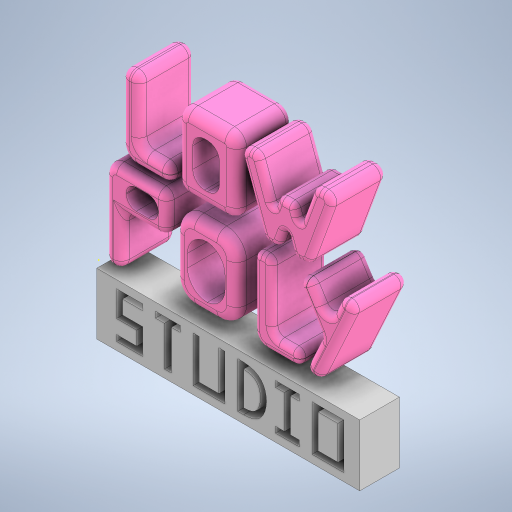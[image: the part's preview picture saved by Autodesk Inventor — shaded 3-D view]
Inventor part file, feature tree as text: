
AUTODESK INVENTOR PART (.ipt)
format: ipt  version: 2024.1 (Build 281209000, 209)  size: 1,081,856 bytes
history: native  units: mm
features: fillet x23, sketch x5, extrude x4, projected_geometry x1
ambient origin geometry x8: Origin, YZ Plane, XZ Plane, XY Plane, X Axis, Y Axis, Z Axis, Center Point
bodies: Solid2 (feature_tree)
feature tree (33):
  extrude  "Extrusion6"  Depth=10.0mm TaperAngle=0.0deg
  extrude  "Extrusion1"  Depth=90.0mm
  extrude  "Extrusion7"  Depth=1.0mm
  fillet  "Fillet1"  Radius=19.198622mm
  fillet  "Fillet2"  Radius=10.0mm
  fillet  "Fillet3"  Radius=28.0mm
  fillet  "Fillet4"  [1 undecoded]
  fillet  "Fillet5"  Radius=4.0mm
  fillet  "Fillet6"  Radius=5.0mm
  fillet  "Fillet7"  Radius=5.0mm
  fillet  "Fillet8"  Radius=10.0mm
  fillet  "Fillet9"  Radius=10.0mm
  fillet  "Fillet10"  Radius=5.0mm
  fillet  "Fillet11"  Radius=3.5mm
  fillet  "Fillet12"  Radius=3.0mm
  fillet  "Fillet13"  Radius=6.0mm
  fillet  "Fillet14"  Radius=3.5mm
  fillet  "Fillet15"  Radius=3.5mm
  fillet  "Fillet16"  Radius=4.0mm
  fillet  "Fillet17"  Radius=4.0mm
  fillet  "Fillet18"  Radius=7.0mm
  fillet  "Fillet19"  Radius=6.0mm
  fillet  "Fillet20"  Radius=6.0mm
  fillet  "Fillet21"  Radius=5.0mm
  fillet  "Fillet22"  Radius=4.0mm
  fillet  "Fillet23"  Radius=1.0mm
  sketch  "Sketch8"  dims[d61=3.0mm d62=3.0mm]
  extrude  "Extrusion8"  Depth=3.0mm
  sketch  "Sketch1"  dims[d0=40.0mm d4=10.0mm d5=0.0mm]
  sketch  "Sketch6"  dims[d24=160.0mm d25=90.0mm]
  projected_geometry  "Projected Loop1"
  sketch  "Sketch7"  dims[d26=90.0mm d27=0.0mm d28=19.198622mm d29=19.198622mm d31=10.0mm d39=28.0mm d40=0.0mm d41=0.0mm d42=4.0mm d43=5.0mm d44=5.0mm d45=10.0mm d46=10.0mm d47=5.0mm d48=3.5mm d49=3.0mm d50=6.0mm d51=3.5mm d52=3.5mm d53=4.0mm d54=4.0mm d55=7.0mm d56=6.0mm d57=6.0mm d58=5.0mm d59=4.0mm d60=1.0mm]
  sketch  "Sketch9"  dims[d63=19.198622mm d64=7.056118mm d65=7.5mm d66=6.0mm d67=3.0mm d69=3.931055mm d70=3.9mm d71=3.0mm d72=3.0mm d73=3.0mm d74=3.0mm d76=3.0mm d77=7.0mm d78=7.0mm d79=3.5mm d80=4.5mm d81=4.5mm d82=3.0mm d83=3.0mm d84=3.0mm d85=10.0mm d86=4.0mm d87=4.0mm d88=4.0mm d89=10.0mm d90=4.0mm d91=4.0mm d92=3.0mm d93=4.5mm d94=4.5mm d97=3.0mm d98=3.0mm d99=3.0mm d100=10.0mm d101=8.0mm d102=6.5mm d103=6.5mm d104=6.5mm d105=8.067383mm d106=5.308861mm d107=8.0mm d108=6.5mm d109=20.0mm d110=0.0mm]
note: 1 required parameter value undecoded (feature->parameter linkage not recoverable at this tier; creation-order binding heuristic only, values carry confidence <= 0.55)
